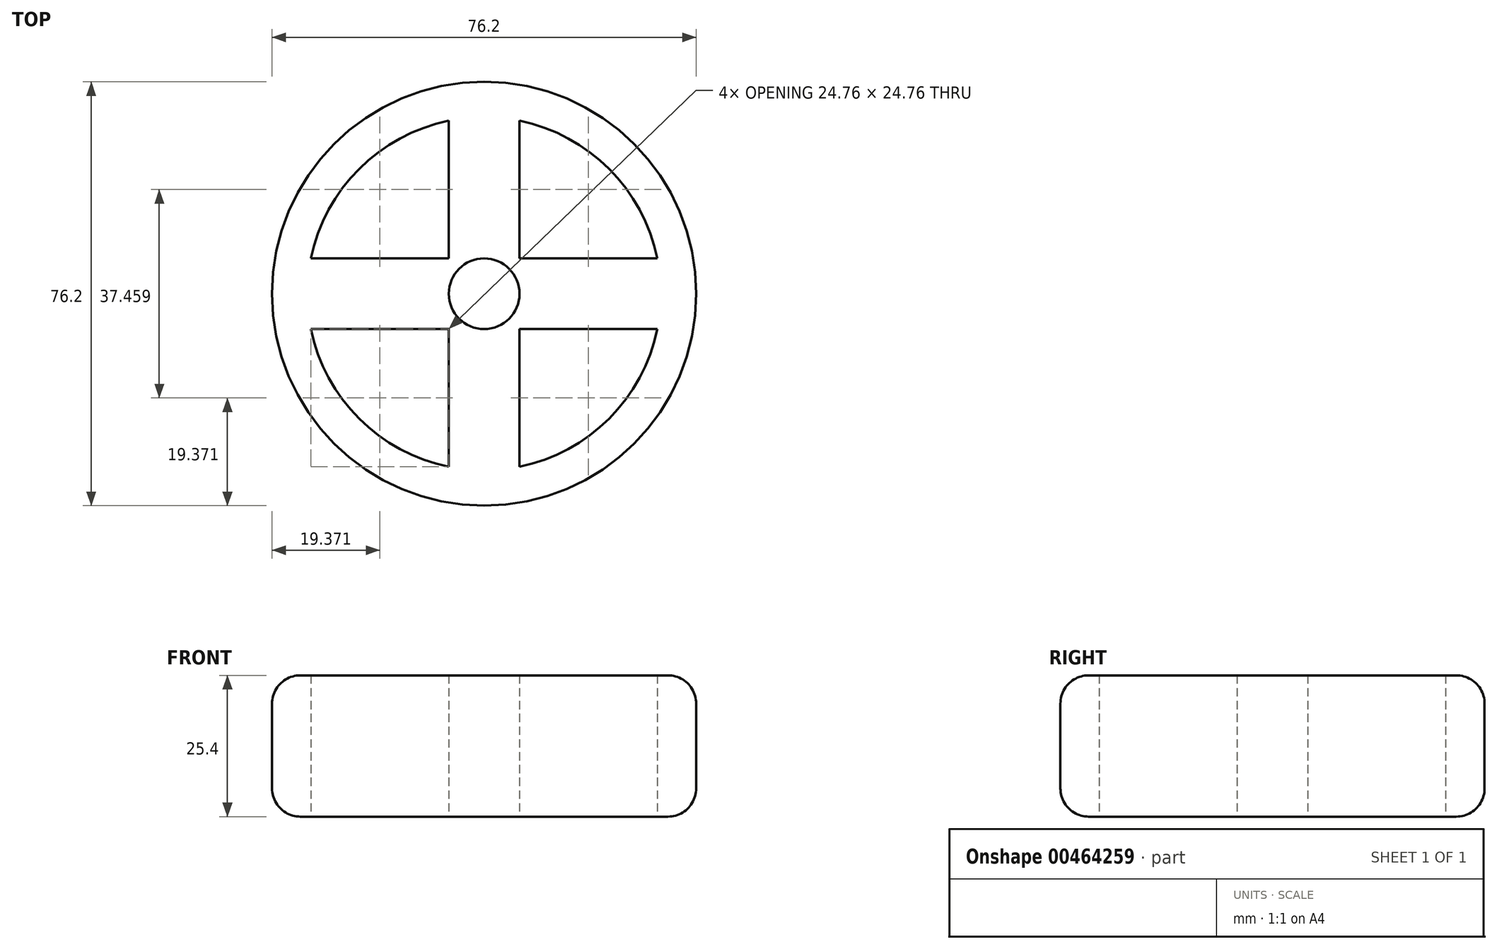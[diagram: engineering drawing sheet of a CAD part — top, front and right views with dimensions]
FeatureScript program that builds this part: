
annotation { "Feature Type Name" : "Feature", "Feature Type Description" : "" }
export const myFeature = defineFeature(function(context is Context, id is Id, definition is map)
    precondition{}
    {
        {
            var Q0;
            Q0=qCreatedBy(makeId("Top.planeOp"),FACE);
            var sketch = newSketch(context, id + "F0", { "sketchPlane" : qUnion([Q0])});
            skCircle(sketch, "E0", {"center": v(0, 0) * mm, "radius": 38.1 * mm});
            skArc(sketch, "E1", {"start": v(31.1, 6.35) * mm, "mid": v(22.45, 22.45) * mm, "end": v(6.35, 31.1) * mm});
            skCircle(sketch, "E2", {"center": v(0, 0) * mm, "radius": 6.35 * mm});
            skCircle(sketch, "E3", {"center": v(0, 0) * mm, "radius": 3.18 * mm});
            skLineSegment(sketch, "E4", {"start": v(0, 0) * mm, "end": v(3.18, 0) * mm});
            skLineSegment(sketch, "E5", {"start": v(0, 0) * mm, "end": v(-3.18, 0) * mm});
            skLineSegment(sketch, "E6", {"start": v(-6.35, 6.35) * mm, "end": v(-6.35, 31.1) * mm});
            skLineSegment(sketch, "E7", {"start": v(6.35, 6.35) * mm, "end": v(6.35, 31.1) * mm});
            skLineSegment(sketch, "E8", {"start": v(-6.35, 6.35) * mm, "end": v(-31.1, 6.35) * mm});
            skLineSegment(sketch, "E9", {"start": v(-6.35, -6.35) * mm, "end": v(-31.1, -6.35) * mm});
            skLineSegment(sketch, "E10", {"start": v(-6.35, -6.35) * mm, "end": v(-6.35, -31.1) * mm});
            skLineSegment(sketch, "E11", {"start": v(6.35, -6.35) * mm, "end": v(6.35, -31.1) * mm});
            skLineSegment(sketch, "E12", {"start": v(6.35, -6.35) * mm, "end": v(31.1, -6.35) * mm});
            skLineSegment(sketch, "E13", {"start": v(6.35, 6.35) * mm, "end": v(31.1, 6.35) * mm});
            skArc(sketch, "E14.trimOffspring", {"start": v(-31.1, -6.35) * mm, "mid": v(-22.45, -22.45) * mm, "end": v(-6.35, -31.1) * mm});
            skArc(sketch, "E15.trimOffspring", {"start": v(6.35, -31.1) * mm, "mid": v(22.45, -22.45) * mm, "end": v(31.1, -6.35) * mm});
            skArc(sketch, "E16.trimOffspring", {"start": v(-6.35, 31.1) * mm, "mid": v(-22.45, 22.45) * mm, "end": v(-31.1, 6.35) * mm});
            skPoint(sketch, "E17.orphan", {"position": v(-6.35, 0) * mm});
            skPoint(sketch, "E18.orphan", {"position": v(0, 6.35) * mm});
            skSolve(sketch);
        }
        {
            var Q0;
            Q0 = qSketchRegion(id + "F0", true);
            extrude(context, id + "F1", {"entities" : qUnion([Q0]), "depth" : 25.4 * mm});
        }
        {
            var Q0;
            Q0=makeQuery(id+"F1.opExtrude","SWEPT_FACE",FACE,{"disambiguationData":[OSD([sQuery(id+"F0.wireOp",EDGE,"E0")])]});
            fillet(context, id + "F2", {"entities" : qUnion([Q0]), "radius" : 5.08 * mm, "tangentPropagation" : true, "allowEdgeOverflow" : false});
        }
    });
